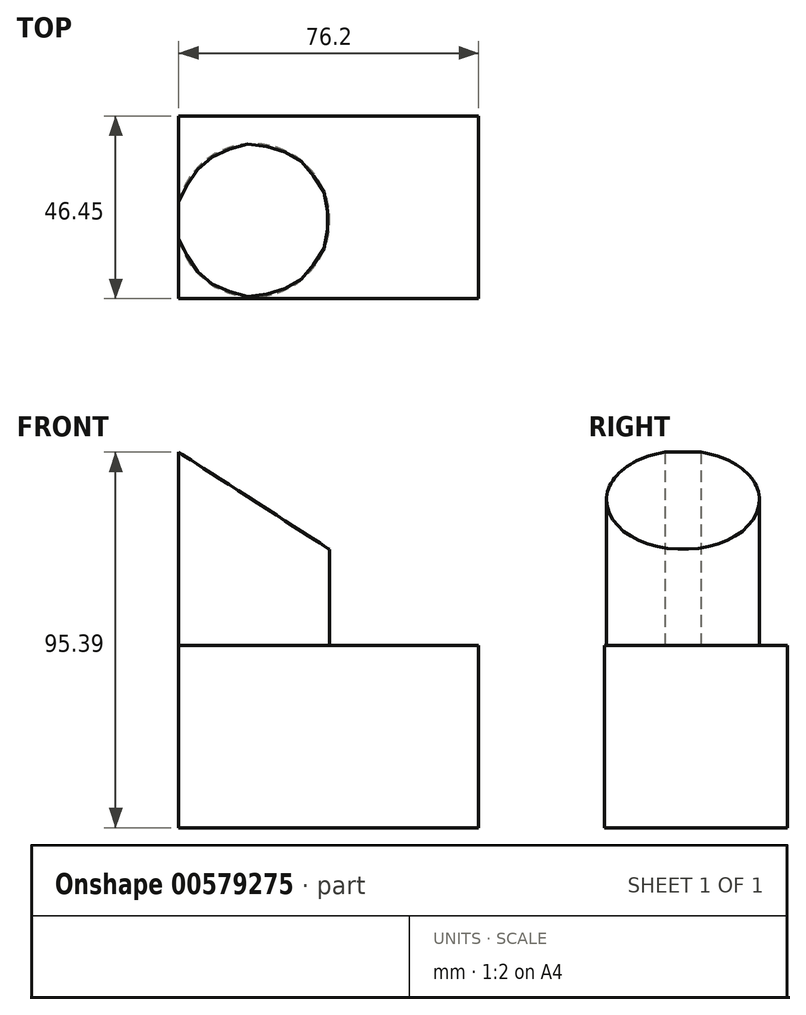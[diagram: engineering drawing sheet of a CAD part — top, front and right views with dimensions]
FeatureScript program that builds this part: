
annotation { "Feature Type Name" : "Feature", "Feature Type Description" : "" }
export const myFeature = defineFeature(function(context is Context, id is Id, definition is map)
    precondition{}
    {
        {
            var Q0;
            Q0=qCreatedBy(makeId("Right.planeOp"),FACE);
            var sketch = newSketch(context, id + "F0", { "sketchPlane" : qUnion([Q0])});
            skLineSegment(sketch, "E0.bottom", {"start": v(23.41, 23.23) * mm, "end": v(-23.04, 23.23) * mm});
            skLineSegment(sketch, "E0.top", {"start": v(23.41, -23.04) * mm, "end": v(-23.04, -23.04) * mm});
            skLineSegment(sketch, "E0.left", {"start": v(23.41, 23.23) * mm, "end": v(23.41, -23.04) * mm});
            skLineSegment(sketch, "E0.right", {"start": v(-23.04, 23.23) * mm, "end": v(-23.04, -23.04) * mm});
            skSolve(sketch);
        }
        {
            var Q0;
            Q0=makeQuery(id+"F0.imprint","IMPRINT",FACE,{"disambiguationData":[TD([[makeQuery(id+"F0.imprint","IMPRINT",EDGE,{"derivedFrom":sQuery(id+"F0.wireOp",EDGE,"E0.bottom")}),1.0]])]});
            extrude(context, id + "F1", {"entities" : qUnion([Q0]), "depth" : 76.2 * mm, "offsetDistance" : 25.4 * mm});
        }
        {
            var Q0;
            Q0=makeQuery(id+"F1.opExtrude","SWEPT_FACE",FACE,{"disambiguationData":[OSD([sQuery(id+"F0.wireOp",EDGE,"E0.bottom")])]});
            var sketch = newSketch(context, id + "F2", { "sketchPlane" : qUnion([Q0])});
            skCircle(sketch, "E1", {"center": v(18.9, -3.13) * mm, "radius": 19.45 * mm});
            skPoint(sketch, "E1.first.point", {"position": v(38.1, 0) * mm});
            skPoint(sketch, "E1.first.point.positionSnap0", {"position": v(38.1, -23.04) * mm});
            skPoint(sketch, "E1.second.point", {"position": v(0, -7.72) * mm});
            skPoint(sketch, "E1.third.point", {"position": v(38.1, -6.26) * mm});
            skPoint(sketch, "E1.third.point.positionSnap0", {"position": v(38.1, -23.04) * mm});
            skSolve(sketch);
        }
        {
            var Q0;
            Q0=makeQuery(id+"F1.opExtrude","CAP_EDGE",EDGE,{"disambiguationData":[OSD([sQuery(id+"F0.wireOp",EDGE,"E0.bottom")])],"isStart":false});
            var Q1;
            {var subQ0=sQuery(id+"F2.wireOp",EDGE,"E1");var subQ1=sQuery(id+"F0.wireOp",EDGE,"E0.bottom");Q1=makeQuery(id+"F4.opExtrude","CAP_VERTEX",VERTEX,{"disambiguationData":[OSD([subQ1,subQ0]),TDD([makeQuery(id+"F2.imprint","INTERSECT",VERTEX,{"disambiguationData":[OD(1.0)],"derivedFrom":[makeQuery(id+"F1.opExtrude","CAP_EDGE",EDGE,{"disambiguationData":[OSD([subQ1])],"isStart":true}),subQ0]})])],"isStart":false});}
            cPlane(context, id + "F3", {"entities" : qUnion([Q0, Q1]), "cplaneType" : CPlaneType.LINE_ANGLE, "offset" : 25.4 * mm, "angle" : 32.8 * degree, "oppositeDirection" : true, "width" : 152.4 * mm, "height" : 152.4 * mm});
        }
        {
            var Q0;
            {var subQ0=sQuery(id+"F2.wireOp",EDGE,"E1");var subQ1=makeQuery(id+"F1.opExtrude","CAP_EDGE",EDGE,{"disambiguationData":[OSD([sQuery(id+"F0.wireOp",EDGE,"E0.bottom")])],"isStart":true});var subQ2=makeQuery(id+"F2.imprint","INTERSECT",VERTEX,{"disambiguationData":[OD(0.0)],"derivedFrom":[subQ1,subQ0]});Q0=makeQuery(id+"F2.imprint","IMPRINT",FACE,{"disambiguationData":[TD([[makeQuery(id+"F2.imprint","IMPRINT",EDGE,{"disambiguationData":[TD([[subQ2,1.0]])],"derivedFrom":subQ0}),1.0]])]});}
            var Q1;
            Q1=qCreatedBy(id+"F3.planeOp",FACE);
            extrude(context, id + "F4", {"entities" : qUnion([Q0]), "operationType" : NewBodyOperationType.ADD, "endBound" : BoundingType.UP_TO_SURFACE, "depth" : 12.7 * mm, "endBoundEntityFace" : qUnion([Q1]), "offsetDistance" : 25.4 * mm});
        }
    });
